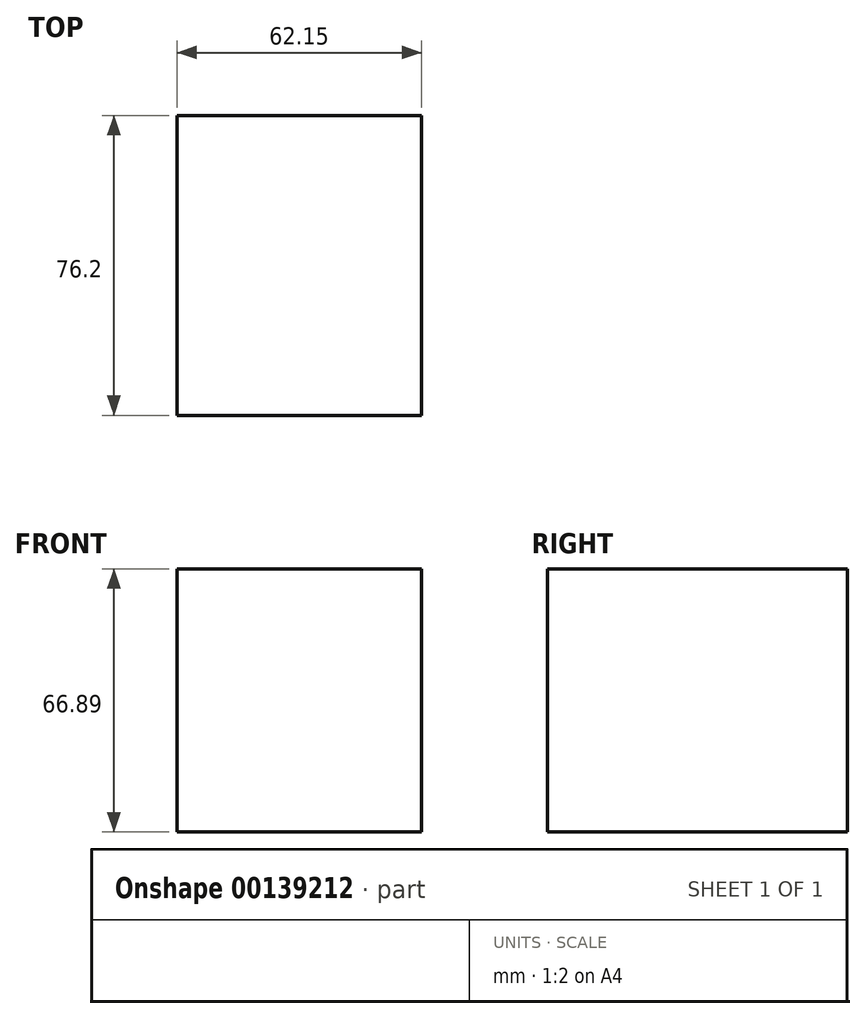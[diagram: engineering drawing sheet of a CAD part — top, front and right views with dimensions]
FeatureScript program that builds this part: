
annotation { "Feature Type Name" : "Feature", "Feature Type Description" : "" }
export const myFeature = defineFeature(function(context is Context, id is Id, definition is map)
    precondition{}
    {
        {
            var Q0;
            Q0=qCreatedBy(makeId("Front.planeOp"),FACE);
            var sketch = newSketch(context, id + "F0", { "sketchPlane" : qUnion([Q0])});
            skLineSegment(sketch, "E0.bottom", {"start": v(-30.19, 37.79) * mm, "end": v(31.96, 37.79) * mm});
            skLineSegment(sketch, "E0.top", {"start": v(-30.19, -29.1) * mm, "end": v(31.96, -29.1) * mm});
            skLineSegment(sketch, "E0.left", {"start": v(-30.19, 37.79) * mm, "end": v(-30.19, -29.1) * mm});
            skLineSegment(sketch, "E0.right", {"start": v(31.96, 37.79) * mm, "end": v(31.96, -29.1) * mm});
            skSolve(sketch);
        }
        {
            var Q0;
            Q0 = qSketchRegion(id + "F0", true);
            extrude(context, id + "F1", {"entities" : qUnion([Q0]), "depth" : 76.2 * mm});
        }
    });
